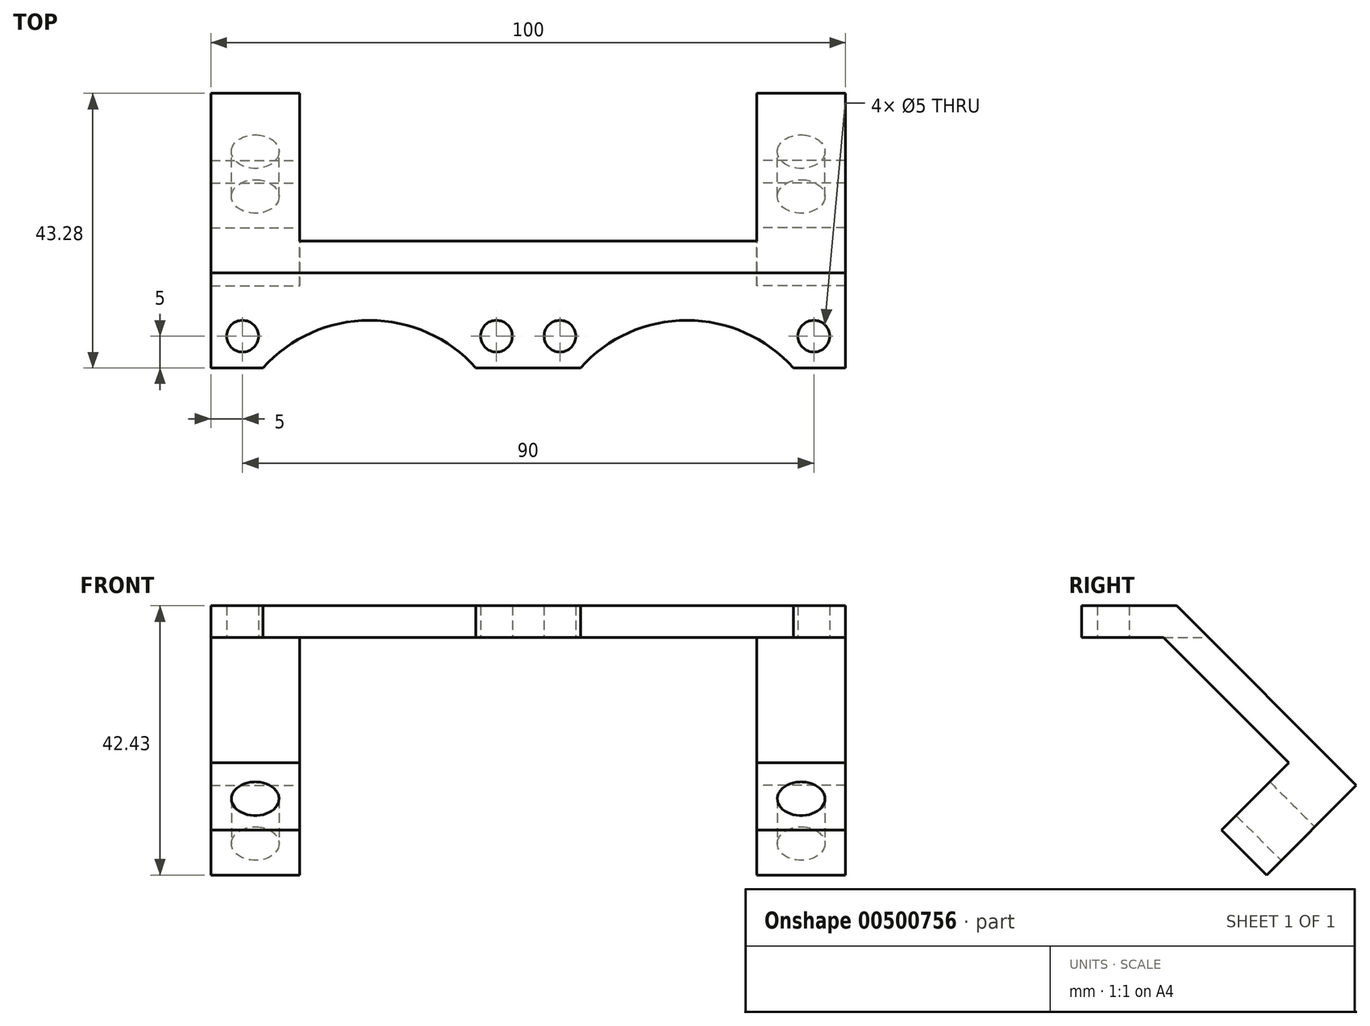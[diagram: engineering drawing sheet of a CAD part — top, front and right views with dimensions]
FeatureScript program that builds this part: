
annotation { "Feature Type Name" : "Feature", "Feature Type Description" : "" }
export const myFeature = defineFeature(function(context is Context, id is Id, definition is map)
    precondition{}
    {
        {
            var Q0;
            Q0=qCreatedBy(makeId("Top.planeOp"),FACE);
            var sketch = newSketch(context, id + "F0", { "sketchPlane" : qUnion([Q0])});
            skLineSegment(sketch, "E0.bottom", {"start": v(-50, 10) * mm, "end": v(50, 10) * mm});
            skLineSegment(sketch, "E0.top", {"start": v(-50, 0) * mm, "end": v(50, 0) * mm});
            skLineSegment(sketch, "E0.left", {"start": v(-50, 10) * mm, "end": v(-50, 0) * mm});
            skLineSegment(sketch, "E0.right", {"start": v(50, 10) * mm, "end": v(50, 0) * mm});
            skCircle(sketch, "E1", {"center": v(-45, 5) * mm, "radius": 2.5 * mm});
            skCircle(sketch, "E2", {"center": v(45, 5) * mm, "radius": 2.5 * mm});
            skCircle(sketch, "E3", {"center": v(5, 5) * mm, "radius": 2.5 * mm});
            skCircle(sketch, "E4", {"center": v(-5, 5) * mm, "radius": 2.5 * mm});
            skCircle(sketch, "E5", {"center": v(-25, -15) * mm, "radius": 22.5 * mm});
            skCircle(sketch, "E6", {"center": v(25, -15) * mm, "radius": 22.5 * mm});
            skLineSegment(sketch, "E7.top", {"start": v(-50, 15) * mm, "end": v(50, 15) * mm});
            skLineSegment(sketch, "E7.left", {"start": v(-50, 10) * mm, "end": v(-50, 15) * mm});
            skLineSegment(sketch, "E7.right", {"start": v(50, 10) * mm, "end": v(50, 15) * mm});
            skSolve(sketch);
        }
        {
            var Q0;
            Q0=makeQuery(id+"F0.imprint","IMPRINT",FACE,{"disambiguationData":[TD([[makeQuery(id+"F0.imprint","IMPRINT",EDGE,{"derivedFrom":sQuery(id+"F0.wireOp",EDGE,"E0.bottom")}),-1.0]])]});
            var Q1;
            Q1=makeQuery(id+"F0.imprint","IMPRINT",FACE,{"disambiguationData":[TD([[makeQuery(id+"F0.imprint","IMPRINT",EDGE,{"derivedFrom":sQuery(id+"F0.wireOp",EDGE,"E0.bottom")}),1.0]])]});
            var Q2;
            {var subQ5=sQuery(id+"F0.wireOp",EDGE,"E0.left");Q2=makeQuery(id+"F0.imprint","IMPRINT",FACE,{"disambiguationData":[TD([[makeQuery(id+"F0.imprint","IMPRINT",EDGE,{"derivedFrom":subQ5}),1.0]])]});}
            extrude(context, id + "F1", {"entities" : qUnion([Q0, Q1, Q2]), "depth" : 5 * mm});
        }
        {
            var Q0;
            Q0=qCreatedBy(makeId("Right.planeOp"),FACE);
            var sketch = newSketch(context, id + "F2", { "sketchPlane" : qUnion([Q0])});
            skLineSegment(sketch, "E8", {"start": v(15, 5) * mm, "end": v(36.21, -16.21) * mm});
            skLineSegment(sketch, "E9", {"start": v(36.21, -16.21) * mm, "end": v(22.07, -30.36) * mm});
            skLineSegment(sketch, "E10", {"start": v(22.07, -30.36) * mm, "end": v(29.14, -37.43) * mm});
            skLineSegment(sketch, "E11", {"start": v(29.14, -37.43) * mm, "end": v(43.28, -23.28) * mm});
            skLineSegment(sketch, "E12", {"start": v(43.28, -23.28) * mm, "end": v(36.21, -16.21) * mm});
            skLineSegment(sketch, "E13", {"start": v(32.68, -19.75) * mm, "end": v(12.93, 0) * mm});
            skLineSegment(sketch, "E14", {"start": v(15, 5) * mm, "end": v(12.93, 0) * mm});
            skSolve(sketch);
        }
        {
            var Q0;
            {var subQ0=sQuery(id+"F2.wireOp",EDGE,"E8");Q0=makeQuery(id+"F2.imprint","IMPRINT",FACE,{"disambiguationData":[TD([[makeQuery(id+"F2.imprint","IMPRINT",EDGE,{"derivedFrom":subQ0}),-1.0]])]});}
            var Q1;
            {var subQ0=sQuery(id+"F2.wireOp",EDGE,"E10");Q1=makeQuery(id+"F2.imprint","IMPRINT",FACE,{"disambiguationData":[TD([[makeQuery(id+"F2.imprint","IMPRINT",EDGE,{"derivedFrom":subQ0}),1.0]])]});}
            extrude(context, id + "F3", {"entities" : qUnion([Q0, Q1]), "operationType" : NewBodyOperationType.ADD, "depth" : 50 * mm, "hasSecondDirection" : true, "secondDirectionOppositeDirection" : false, "secondDirectionDepth" : 36 * mm});
        }
        {
            var Q0;
            {var subQ0=sQuery(id+"F2.wireOp",EDGE,"E8");Q0=makeQuery(id+"F2.imprint","IMPRINT",FACE,{"disambiguationData":[TD([[makeQuery(id+"F2.imprint","IMPRINT",EDGE,{"derivedFrom":subQ0}),-1.0]])]});}
            var Q1;
            {var subQ0=sQuery(id+"F2.wireOp",EDGE,"E10");Q1=makeQuery(id+"F2.imprint","IMPRINT",FACE,{"disambiguationData":[TD([[makeQuery(id+"F2.imprint","IMPRINT",EDGE,{"derivedFrom":subQ0}),1.0]])]});}
            extrude(context, id + "F4", {"entities" : qUnion([Q0, Q1]), "operationType" : NewBodyOperationType.ADD, "oppositeDirection" : true, "depth" : 50 * mm, "hasSecondDirection" : true, "secondDirectionOppositeDirection" : true, "secondDirectionDepth" : 36 * mm});
        }
        {
            var Q0;
            Q0=makeQuery(id+"F4.opExtrude","SWEPT_FACE",FACE,{"disambiguationData":[OSD([sQuery(id+"F2.wireOp",EDGE,"E11")])]});
            var sketch = newSketch(context, id + "F5", { "sketchPlane" : qUnion([Q0])});
            skCircle(sketch, "E15", {"center": v(43, 1.14) * mm, "radius": 3.75 * mm});
            skCircle(sketch, "E16", {"center": v(-43, 1.14) * mm, "radius": 3.75 * mm});
            skSolve(sketch);
        }
        {
            var Q0;
            Q0=makeQuery(id+"F5.imprint","IMPRINT",FACE,{"disambiguationData":[TD([[makeQuery(id+"F5.imprint","IMPRINT",EDGE,{"derivedFrom":sQuery(id+"F5.wireOp",EDGE,"E15")}),1.0]])]});
            var Q1;
            Q1=makeQuery(id+"F5.imprint","IMPRINT",FACE,{"disambiguationData":[TD([[makeQuery(id+"F5.imprint","IMPRINT",EDGE,{"derivedFrom":sQuery(id+"F5.wireOp",EDGE,"E16")}),1.0]])]});
            extrude(context, id + "F6", {"entities" : qUnion([Q0, Q1]), "operationType" : NewBodyOperationType.REMOVE, "oppositeDirection" : true, "depth" : 10 * mm});
        }
        {
            var Q0;
            Q0=qCreatedBy(makeId("Right.planeOp"),FACE);
            var sketch = newSketch(context, id + "F7", { "sketchPlane" : qUnion([Q0])});
            skLineSegment(sketch, "E17", {"start": v(15, 5) * mm, "end": v(15, 0) * mm});
            skLineSegment(sketch, "E18", {"start": v(15, 0) * mm, "end": v(20, 0) * mm});
            skLineSegment(sketch, "E19", {"start": v(20, 0) * mm, "end": v(15, 5) * mm});
            skSolve(sketch);
        }
        {
            var Q0;
            Q0=makeQuery(id+"F7.imprint","IMPRINT",FACE,{"disambiguationData":[TD([[makeQuery(id+"F7.imprint","IMPRINT",EDGE,{"derivedFrom":sQuery(id+"F7.wireOp",EDGE,"E17")}),1.0]])]});
            extrude(context, id + "F8", {"entities" : qUnion([Q0]), "operationType" : NewBodyOperationType.ADD, "depth" : 100 * mm, "symmetric" : true});
        }
    });
